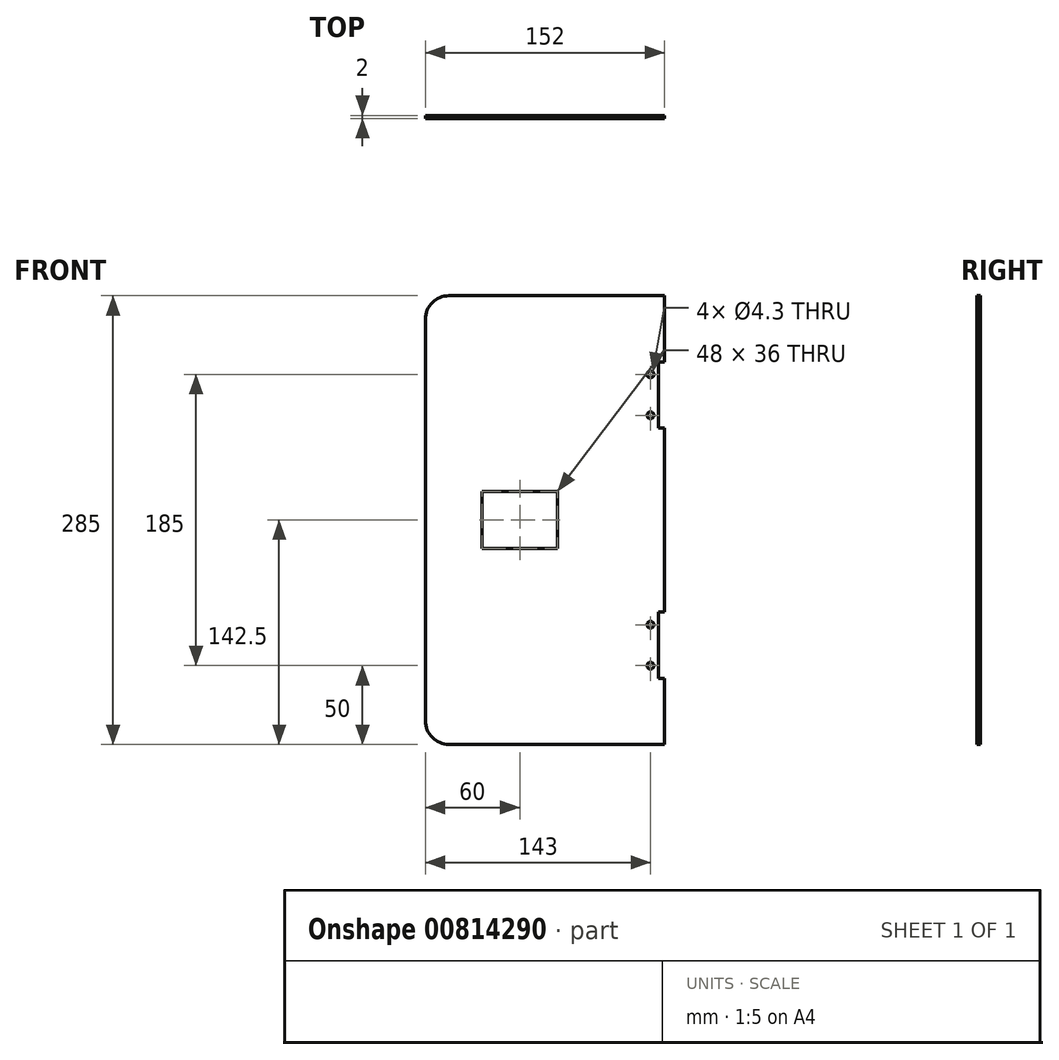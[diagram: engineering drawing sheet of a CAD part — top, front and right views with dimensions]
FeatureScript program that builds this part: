
annotation { "Feature Type Name" : "Feature", "Feature Type Description" : "" }
export const myFeature = defineFeature(function(context is Context, id is Id, definition is map)
    precondition{}
    {
        {
            var Q0;
            Q0=qCreatedBy(makeId("Front.planeOp"),FACE);
            var sketch = newSketch(context, id + "F0", { "sketchPlane" : qUnion([Q0])});
            skLineSegment(sketch, "E0.bottom", {"start": v(74, 142.5) * mm, "end": v(-74, 142.5) * mm});
            skLineSegment(sketch, "E0.top", {"start": v(74, -142.5) * mm, "end": v(-74, -142.5) * mm});
            skLineSegment(sketch, "E0.left", {"start": v(74, 142.5) * mm, "end": v(74, -142.5) * mm});
            skLineSegment(sketch, "E0.right", {"start": v(-74, 142.5) * mm, "end": v(-74, -142.5) * mm});
            skPoint(sketch, "E0.middle", {"position": v(0, 0) * mm});
            skLineSegment(sketch, "E1.bottom", {"start": v(74, 142.5) * mm, "end": v(78, 142.5) * mm});
            skLineSegment(sketch, "E1.top", {"start": v(74, 100.5) * mm, "end": v(78, 100.5) * mm});
            skLineSegment(sketch, "E1.left", {"start": v(74, 142.5) * mm, "end": v(74, 100.5) * mm});
            skLineSegment(sketch, "E1.right", {"start": v(78, 142.5) * mm, "end": v(78, 100.5) * mm});
            skLineSegment(sketch, "E2.bottom", {"start": v(74, -142.5) * mm, "end": v(78, -142.5) * mm});
            skLineSegment(sketch, "E2.top", {"start": v(74, -100.5) * mm, "end": v(78, -100.5) * mm});
            skLineSegment(sketch, "E2.left", {"start": v(74, -142.5) * mm, "end": v(74, -100.5) * mm});
            skLineSegment(sketch, "E2.right", {"start": v(78, -142.5) * mm, "end": v(78, -100.5) * mm});
            skLineSegment(sketch, "E3.bottom", {"start": v(78, 58.5) * mm, "end": v(74, 58.5) * mm});
            skLineSegment(sketch, "E3.top", {"start": v(78, -58.5) * mm, "end": v(74, -58.5) * mm});
            skLineSegment(sketch, "E3.left", {"start": v(78, 58.5) * mm, "end": v(78, -58.5) * mm});
            skLineSegment(sketch, "E3.right", {"start": v(74, 58.5) * mm, "end": v(74, -58.5) * mm});
            skSolve(sketch);
        }
        {
            var Q0;
            Q0 = qSketchRegion(id + "F0", true);
            extrude(context, id + "F1", {"entities" : qUnion([Q0]), "depth" : 2 * mm, "offsetDistance" : 25 * mm, "symmetric" : true});
        }
        {
            var Q0;
            Q0=makeQuery(id+"F1.opExtrude","SWEPT_EDGE",EDGE,{"disambiguationData":[OSD([sQuery(id+"F0.wireOp",EDGE,"E0.bottom"),sQuery(id+"F0.wireOp",EDGE,"E0.right")])]});
            var Q1;
            Q1=makeQuery(id+"F1.opExtrude","SWEPT_EDGE",EDGE,{"disambiguationData":[OSD([sQuery(id+"F0.wireOp",EDGE,"E0.top"),sQuery(id+"F0.wireOp",EDGE,"E0.right")])]});
            fillet(context, id + "F2", {"entities" : qUnion([Q0, Q1]), "radius" : 15 * mm, "tangentPropagation" : true, "allowEdgeOverflow" : false});
        }
        {
            var Q0;
            Q0=makeQuery(id+"F1.opExtrude","CAP_FACE",FACE,{"disambiguationData":[OSD([sQuery(id+"F0.wireOp",EDGE,"E0.bottom"),sQuery(id+"F0.wireOp",EDGE,"E0.top"),sQuery(id+"F0.wireOp",EDGE,"E0.left"),sQuery(id+"F0.wireOp",EDGE,"E0.right")])],"isStart":true});
            var sketch = newSketch(context, id + "F3", { "sketchPlane" : qUnion([Q0])});
            skPoint(sketch, "E4", {"position": v(-69, 92.5) * mm});
            skPoint(sketch, "E5", {"position": v(-69, 66.5) * mm});
            skPoint(sketch, "E6", {"position": v(-69, -66.5) * mm});
            skPoint(sketch, "E7", {"position": v(-69, -92.5) * mm});
            skSolve(sketch);
        }
        {
            var Q0;
            Q0=sQuery(id+"F3.wireOp",VERTEX,"E4");
            var Q1;
            Q1=sQuery(id+"F3.wireOp",VERTEX,"E5");
            var Q2;
            Q2=sQuery(id+"F3.wireOp",VERTEX,"E7");
            var Q3;
            Q3=sQuery(id+"F3.wireOp",VERTEX,"E6");
            var Q4;
            Q4=makeQuery(id+"F1.opExtrude","SWEPT_BODY",BODY,{"disambiguationData":[OSD([sQuery(id+"F0.wireOp",EDGE,"E0.bottom"),sQuery(id+"F0.wireOp",EDGE,"E0.top"),sQuery(id+"F0.wireOp",EDGE,"E0.left"),sQuery(id+"F0.wireOp",EDGE,"E0.right")])]});
            hole(context, id + "F4", {"style" : HoleStyle.SIMPLE, "endStyle" : HoleEndStyle.BLIND, "holeDiameter" : 4.3 * mm, "majorDiameter" : 5 * mm, "holeDepth" : 4 * mm, "isTappedThrough" : true, "tappedDepth" : 12 * mm, "tapClearance" : 3, "locations" : qUnion([Q0, Q1, Q2, Q3]), "scope" : qUnion([Q4]), "startStyle" : HoleStartStyle.SKETCH});
        }
        {
            var Q0;
            Q0=makeQuery(id+"F1.opExtrude","CAP_FACE",FACE,{"disambiguationData":[OSD([sQuery(id+"F0.wireOp",EDGE,"E0.bottom"),sQuery(id+"F0.wireOp",EDGE,"E0.top"),sQuery(id+"F0.wireOp",EDGE,"E0.left"),sQuery(id+"F0.wireOp",EDGE,"E0.right"),sQuery(id+"F0.wireOp",EDGE,"E1.bottom"),sQuery(id+"F0.wireOp",EDGE,"E1.top"),sQuery(id+"F0.wireOp",EDGE,"E1.right"),sQuery(id+"F0.wireOp",EDGE,"E2.bottom"),sQuery(id+"F0.wireOp",EDGE,"E2.top"),sQuery(id+"F0.wireOp",EDGE,"E2.right"),sQuery(id+"F0.wireOp",EDGE,"E3.bottom"),sQuery(id+"F0.wireOp",EDGE,"E3.top"),sQuery(id+"F0.wireOp",EDGE,"E3.left")])],"isStart":true});
            var sketch = newSketch(context, id + "F5", { "sketchPlane" : qUnion([Q0])});
            skLineSegment(sketch, "E8.bottom", {"start": v(38, 18) * mm, "end": v(-10, 18) * mm});
            skLineSegment(sketch, "E8.top", {"start": v(38, -18) * mm, "end": v(-10, -18) * mm});
            skLineSegment(sketch, "E8.left", {"start": v(38, 18) * mm, "end": v(38, -18) * mm});
            skLineSegment(sketch, "E8.right", {"start": v(-10, 18) * mm, "end": v(-10, -18) * mm});
            skPoint(sketch, "E8.middle", {"position": v(14, 0) * mm});
            skSolve(sketch);
        }
        {
            var Q0;
            Q0=makeQuery(id+"F5.imprint","IMPRINT",FACE,{"disambiguationData":[TD([[makeQuery(id+"F5.imprint","IMPRINT",EDGE,{"derivedFrom":sQuery(id+"F5.wireOp",EDGE,"E8.bottom")}),1.0]])]});
            extrude(context, id + "F6", {"entities" : qUnion([Q0]), "operationType" : NewBodyOperationType.REMOVE, "oppositeDirection" : true, "depth" : 2 * mm, "offsetDistance" : 25 * mm});
        }
    });
